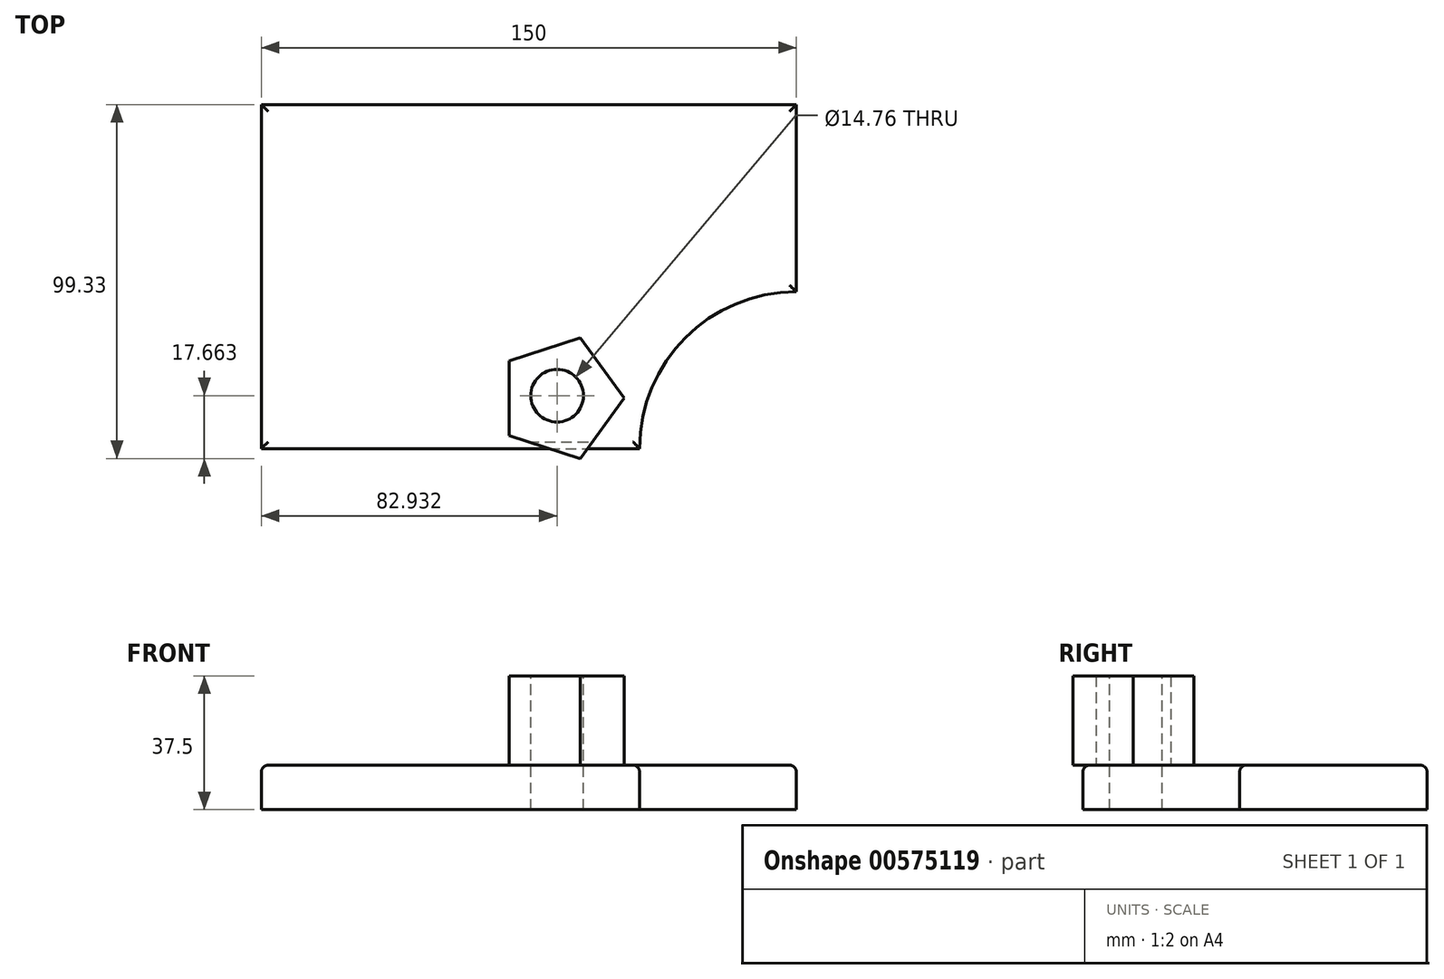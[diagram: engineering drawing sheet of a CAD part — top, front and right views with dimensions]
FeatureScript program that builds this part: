
annotation { "Feature Type Name" : "Feature", "Feature Type Description" : "" }
export const myFeature = defineFeature(function(context is Context, id is Id, definition is map)
    precondition{}
    {
        {
            var Q0;
            Q0=qCreatedBy(makeId("Top.planeOp"),FACE);
            var sketch = newSketch(context, id + "F0", { "sketchPlane" : qUnion([Q0])});
            skLineSegment(sketch, "E0.bottom", {"start": v(-150, 96.5) * mm, "end": v(0, 96.5) * mm});
            skLineSegment(sketch, "E0.top", {"start": v(-150, 0) * mm, "end": v(0, 0) * mm});
            skLineSegment(sketch, "E0.left", {"start": v(-150, 96.5) * mm, "end": v(-150, 0) * mm});
            skLineSegment(sketch, "E0.right", {"start": v(0, 96.5) * mm, "end": v(0, 0) * mm});
            skSolve(sketch);
        }
        {
            var Q0;
            Q0=makeQuery(id+"F0.imprint","IMPRINT",FACE,{"disambiguationData":[TD([[makeQuery(id+"F0.imprint","IMPRINT",EDGE,{"derivedFrom":sQuery(id+"F0.wireOp",EDGE,"E0.bottom")}),-1.0]])]});
            extrude(context, id + "F1", {"entities" : qUnion([Q0]), "depth" : 25 * mm, "offsetDistance" : 25 * mm});
        }
        {
            var Q0;
            Q0=makeQuery(id+"F1.opExtrude","CAP_FACE",FACE,{"disambiguationData":[OSD([sQuery(id+"F0.wireOp",EDGE,"E0.bottom"),sQuery(id+"F0.wireOp",EDGE,"E0.top"),sQuery(id+"F0.wireOp",EDGE,"E0.left"),sQuery(id+"F0.wireOp",EDGE,"E0.right")])],"isStart":false});
            var sketch = newSketch(context, id + "F2", { "sketchPlane" : qUnion([Q0])});
            skCircle(sketch, "E1", {"center": v(0, 0) * mm, "radius": 43.95 * mm});
            skSolve(sketch);
        }
        {
            var Q0;
            Q0=makeQuery(id+"F2.imprint","IMPRINT",FACE,{"disambiguationData":[TD([[makeQuery(id+"F2.imprint","IMPRINT",EDGE,{"derivedFrom":sQuery(id+"F2.wireOp",EDGE,"E1")}),-1.0]])]});
            extrude(context, id + "F3", {"entities" : qUnion([Q0]), "operationType" : NewBodyOperationType.INTERSECT, "endBound" : BoundingType.SYMMETRIC, "depth" : 25 * mm, "offsetDistance" : 25 * mm});
        }
        {
            var Q0;
            Q0=makeQuery(id+"F1.opExtrude","CAP_FACE",FACE,{"disambiguationData":[OSD([sQuery(id+"F0.wireOp",EDGE,"E0.bottom"),sQuery(id+"F0.wireOp",EDGE,"E0.top"),sQuery(id+"F0.wireOp",EDGE,"E0.left"),sQuery(id+"F0.wireOp",EDGE,"E0.right")])],"isStart":false});
            fillet(context, id + "F4", {"entities" : qUnion([Q0]), "tangentPropagation" : true, "radius" : 1.9 * mm, "defaultsChanged" : true, "vertexSettings" : [], "allowEdgeOverflow" : false});
        }
        {
            var Q0;
            Q0=makeQuery(id+"F1.opExtrude","CAP_FACE",FACE,{"disambiguationData":[OSD([sQuery(id+"F0.wireOp",EDGE,"E0.bottom"),sQuery(id+"F0.wireOp",EDGE,"E0.top"),sQuery(id+"F0.wireOp",EDGE,"E0.left"),sQuery(id+"F0.wireOp",EDGE,"E0.right")])],"isStart":false});
            var sketch = newSketch(context, id + "F5", { "sketchPlane" : qUnion([Q0])});
            skCircle(sketch, "E2.cCircle", {"center": v(-66.11, 14.14) * mm, "radius": 14.43 * mm, "construction": true});
            skLineSegment(sketch, "E2.0", {"start": v(-80.54, 3.65) * mm, "end": v(-80.54, 24.62) * mm});
            skLineSegment(sketch, "E2.1", {"start": v(-80.54, 24.62) * mm, "end": v(-60.6, 31.1) * mm});
            skLineSegment(sketch, "E2.2", {"start": v(-60.6, 31.1) * mm, "end": v(-48.28, 14.14) * mm});
            skLineSegment(sketch, "E2.3", {"start": v(-48.28, 14.14) * mm, "end": v(-60.6, -2.83) * mm});
            skLineSegment(sketch, "E2.4", {"start": v(-60.6, -2.83) * mm, "end": v(-80.54, 3.65) * mm});
            skPoint(sketch, "E2.0.midPoint", {"position": v(-80.54, 14.14) * mm});
            skSolve(sketch);
        }
        {
            var Q0;
            Q0 = qSketchRegion(id + "F5", true);
            extrude(context, id + "F6", {"entities" : qUnion([Q0]), "operationType" : NewBodyOperationType.ADD, "depth" : 25 * mm, "offsetDistance" : 25 * mm});
        }
        {
            var Q0;
            Q0=makeQuery(id+"F6.opExtrude","CAP_FACE",FACE,{"disambiguationData":[OSD([sQuery(id+"F5.wireOp",EDGE,"E2.0"),sQuery(id+"F5.wireOp",EDGE,"E2.1"),sQuery(id+"F5.wireOp",EDGE,"E2.2"),sQuery(id+"F5.wireOp",EDGE,"E2.3"),sQuery(id+"F5.wireOp",EDGE,"E2.4")])],"isStart":false});
            var sketch = newSketch(context, id + "F7", { "sketchPlane" : qUnion([Q0])});
            skCircle(sketch, "E3", {"center": v(-67.07, 14.83) * mm, "radius": 7.38 * mm});
            skSolve(sketch);
        }
        {
            var Q0;
            Q0=makeQuery(id+"F7.imprint","IMPRINT",FACE,{"disambiguationData":[TD([[makeQuery(id+"F7.imprint","IMPRINT",EDGE,{"derivedFrom":sQuery(id+"F7.wireOp",EDGE,"E3")}),1.0]])]});
            extrude(context, id + "F8", {"entities" : qUnion([Q0]), "operationType" : NewBodyOperationType.REMOVE, "oppositeDirection" : true, "depth" : 50 * mm, "offsetDistance" : 25 * mm});
        }
    });
